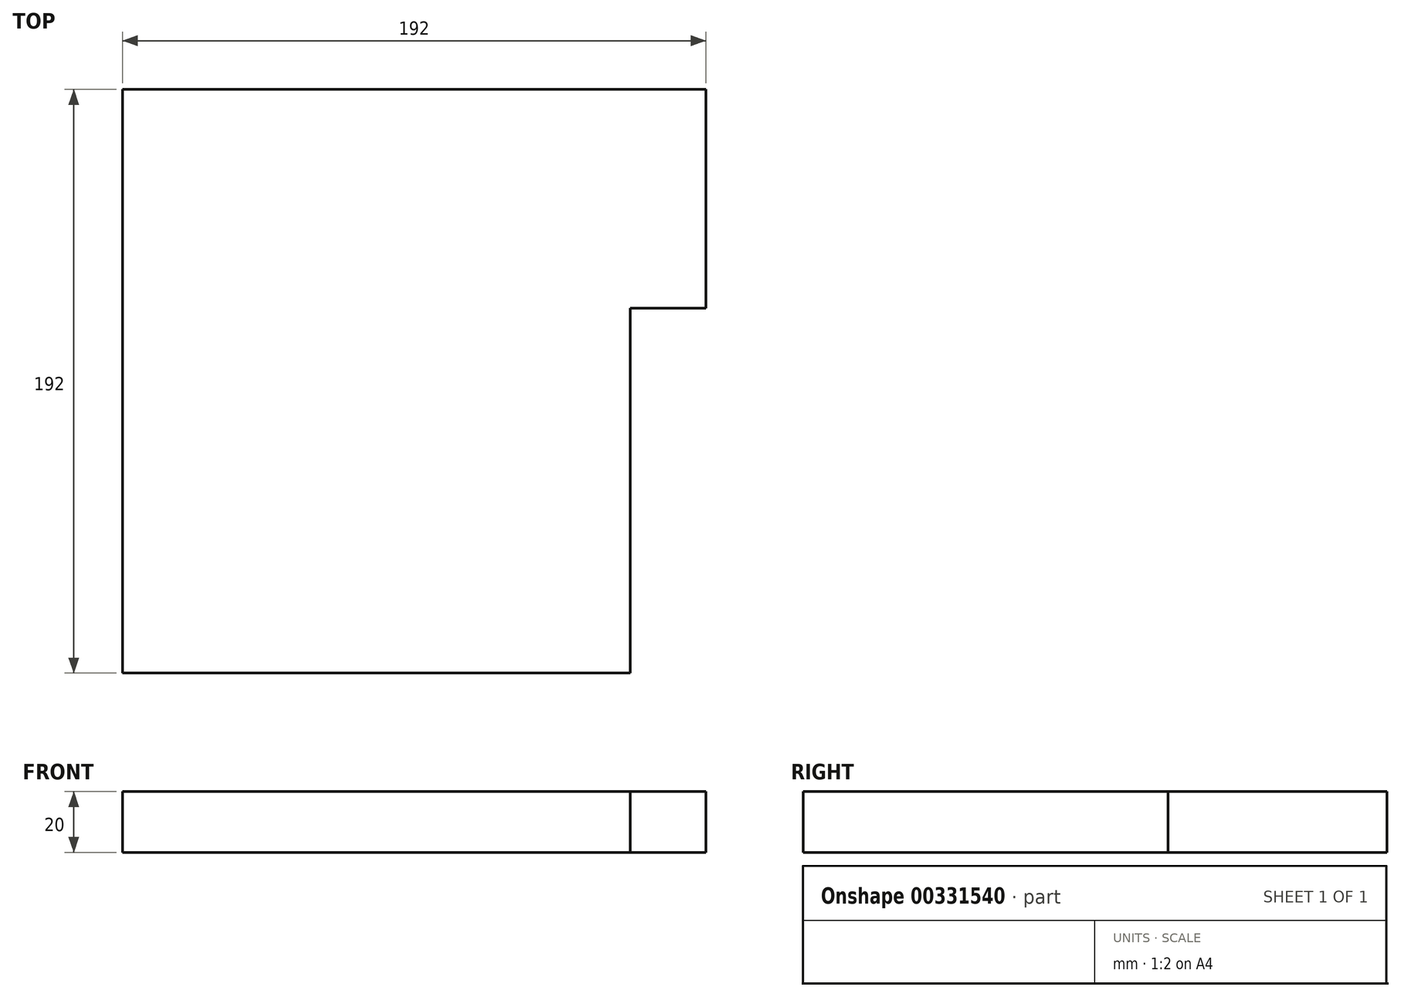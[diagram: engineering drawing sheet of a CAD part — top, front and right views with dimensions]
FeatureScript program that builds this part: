
annotation { "Feature Type Name" : "Feature", "Feature Type Description" : "" }
export const myFeature = defineFeature(function(context is Context, id is Id, definition is map)
    precondition{}
    {
        {
            var Q0;
            Q0=qCreatedBy(makeId("Top.planeOp"),FACE);
            var sketch = newSketch(context, id + "F0", { "sketchPlane" : qUnion([Q0])});
            skLineSegment(sketch, "E0", {"start": v(1313, 440) * mm, "end": v(1313, 406) * mm});
            skLineSegment(sketch, "E1", {"start": v(1313, -267) * mm, "end": v(1313, -301) * mm});
            skLineSegment(sketch, "E2", {"start": v(1313, -301) * mm, "end": v(647, -301) * mm});
            skLineSegment(sketch, "E3", {"start": v(1279, -267) * mm, "end": v(647, -267) * mm});
            skLineSegment(sketch, "E4", {"start": v(1279, 406) * mm, "end": v(688, 406) * mm});
            skLineSegment(sketch, "E5", {"start": v(688, 406) * mm, "end": v(688, -75) * mm});
            skLineSegment(sketch, "E6", {"start": v(688, -75) * mm, "end": v(413, -75) * mm});
            skLineSegment(sketch, "E7", {"start": v(647, -301) * mm, "end": v(647, -267) * mm});
            skLineSegment(sketch, "E8", {"start": v(536, -301) * mm, "end": v(536, -267) * mm});
            skLineSegment(sketch, "E9", {"start": v(536, -267) * mm, "end": v(328, -267) * mm});
            skLineSegment(sketch, "E10", {"start": v(328, -267) * mm, "end": v(328, -407) * mm});
            skLineSegment(sketch, "E11", {"start": v(328, -407) * mm, "end": v(-40, -407) * mm});
            skLineSegment(sketch, "E12", {"start": v(-40, -407) * mm, "end": v(-40, -188) * mm});
            skLineSegment(sketch, "E13", {"start": v(-40, -188) * mm, "end": v(-105, -188) * mm});
            skLineSegment(sketch, "E14", {"start": v(536, -301) * mm, "end": v(362, -301) * mm});
            skLineSegment(sketch, "E15", {"start": v(362, -301) * mm, "end": v(362, -440) * mm});
            skLineSegment(sketch, "E16", {"start": v(-60, -407) * mm, "end": v(-60, -215) * mm});
            skLineSegment(sketch, "E17", {"start": v(-60, -215) * mm, "end": v(-105, -215) * mm});
            skLineSegment(sketch, "E18", {"start": v(-105, -188) * mm, "end": v(-105, -215) * mm});
            skLineSegment(sketch, "E19", {"start": v(-60, -407) * mm, "end": v(-282, -407) * mm});
            skLineSegment(sketch, "E20", {"start": v(-282, -407) * mm, "end": v(-282, -287) * mm});
            skLineSegment(sketch, "E21", {"start": v(-282, -287) * mm, "end": v(-330, -287) * mm});
            skLineSegment(sketch, "E22", {"start": v(-330, -287) * mm, "end": v(-330, -407) * mm});
            skLineSegment(sketch, "E23", {"start": v(-330, -407) * mm, "end": v(-497, -407) * mm});
            skLineSegment(sketch, "E24", {"start": v(-197, -188) * mm, "end": v(-197, -215) * mm});
            skLineSegment(sketch, "E25", {"start": v(-197, -188) * mm, "end": v(-765, -188) * mm});
            skLineSegment(sketch, "E26", {"start": v(-197, -215) * mm, "end": v(-497, -215) * mm});
            skLineSegment(sketch, "E27", {"start": v(-497, -215) * mm, "end": v(-497, -231) * mm});
            skLineSegment(sketch, "E28", {"start": v(-497, -231) * mm, "end": v(-497, -293) * mm});
            skLineSegment(sketch, "E29", {"start": v(-497, -407) * mm, "end": v(-497, -349) * mm});
            skLineSegment(sketch, "E30", {"start": v(413, -75) * mm, "end": v(413, -54) * mm});
            skLineSegment(sketch, "E31", {"start": v(413, -54) * mm, "end": v(667, -54) * mm});
            skLineSegment(sketch, "E32", {"start": v(667, -54) * mm, "end": v(667, 406) * mm});
            skLineSegment(sketch, "E33", {"start": v(667, 406) * mm, "end": v(495, 406) * mm});
            skLineSegment(sketch, "E34", {"start": v(312, 406) * mm, "end": v(391, 406) * mm});
            skLineSegment(sketch, "E35", {"start": v(391, 406) * mm, "end": v(391, 440) * mm});
            skLineSegment(sketch, "E36", {"start": v(495, 406) * mm, "end": v(495, 440) * mm});
            skLineSegment(sketch, "E37", {"start": v(1313, 440) * mm, "end": v(495, 440) * mm});
            skLineSegment(sketch, "E38", {"start": v(312, -75) * mm, "end": v(60, -75) * mm});
            skLineSegment(sketch, "E39", {"start": v(-1279, 406) * mm, "end": v(-1279, 7) * mm});
            skLineSegment(sketch, "E40", {"start": v(-790, 406) * mm, "end": v(-790, 7) * mm});
            skLineSegment(sketch, "E41", {"start": v(-1279, 7) * mm, "end": v(-910, 7) * mm});
            skLineSegment(sketch, "E42", {"start": v(-790, 7) * mm, "end": v(-808, 7) * mm});
            skLineSegment(sketch, "E43", {"start": v(-765, -188) * mm, "end": v(-765, -208) * mm});
            skLineSegment(sketch, "E44", {"start": v(290, 141) * mm, "end": v(290, 406) * mm});
            skLineSegment(sketch, "E45", {"start": v(290, 141) * mm, "end": v(75, 141) * mm});
            skLineSegment(sketch, "E46", {"start": v(75, -46) * mm, "end": v(75, 141) * mm});
            skLineSegment(sketch, "E47", {"start": v(60, -75) * mm, "end": v(60, -46) * mm});
            skLineSegment(sketch, "E48", {"start": v(391, 406) * mm, "end": v(312, 406) * mm});
            skLineSegment(sketch, "E49", {"start": v(-139, 406) * mm, "end": v(-139, 440) * mm});
            skLineSegment(sketch, "E50", {"start": v(-318, 406) * mm, "end": v(-318, 440) * mm});
            skLineSegment(sketch, "E51", {"start": v(-515, 406) * mm, "end": v(-515, 440) * mm});
            skLineSegment(sketch, "E52", {"start": v(-694, 406) * mm, "end": v(-694, 440) * mm});
            skLineSegment(sketch, "E53", {"start": v(-770, 406) * mm, "end": v(-770, 9) * mm});
            skLineSegment(sketch, "E54", {"start": v(-694, 406) * mm, "end": v(-770, 406) * mm});
            skLineSegment(sketch, "E55", {"start": v(75, 406) * mm, "end": v(-139, 406) * mm});
            skLineSegment(sketch, "E56", {"start": v(-318, 406) * mm, "end": v(-515, 406) * mm});
            skLineSegment(sketch, "E57", {"start": v(-318, 440) * mm, "end": v(-515, 440) * mm});
            skLineSegment(sketch, "E58", {"start": v(-770, 9) * mm, "end": v(-754, 9) * mm});
            skLineSegment(sketch, "E59", {"start": v(-677, 9) * mm, "end": v(-659, 9) * mm});
            skLineSegment(sketch, "E60", {"start": v(-659, 9) * mm, "end": v(-659, -5) * mm});
            skLineSegment(sketch, "E61", {"start": v(-659, -5) * mm, "end": v(-659, -46) * mm});
            skLineSegment(sketch, "E62", {"start": v(-659, -46) * mm, "end": v(-60, -46) * mm});
            skLineSegment(sketch, "E63", {"start": v(-60, -75) * mm, "end": v(-60, -46) * mm});
            skLineSegment(sketch, "E64", {"start": v(60, -75) * mm, "end": v(128, -75) * mm});
            skLineSegment(sketch, "E65", {"start": v(60, -46) * mm, "end": v(75, -46) * mm});
            skLineSegment(sketch, "E66", {"start": v(96, -46) * mm, "end": v(290, -46) * mm});
            skLineSegment(sketch, "E67", {"start": v(-60, -75) * mm, "end": v(-677, -75) * mm});
            skLineSegment(sketch, "E68", {"start": v(-677, 9) * mm, "end": v(-677, -75) * mm});
            skLineSegment(sketch, "E69", {"start": v(-754, 9) * mm, "end": v(-754, -13) * mm});
            skLineSegment(sketch, "E70", {"start": v(-808, 7) * mm, "end": v(-808, -13) * mm});
            skLineSegment(sketch, "E71", {"start": v(-808, -13) * mm, "end": v(-754, -13) * mm});
            skLineSegment(sketch, "E72", {"start": v(-910, 7) * mm, "end": v(-910, -29) * mm});
            skLineSegment(sketch, "E73", {"start": v(-1279, -406) * mm, "end": v(-935, -406) * mm});
            skLineSegment(sketch, "E74", {"start": v(-1313, -440) * mm, "end": v(-935, -440) * mm});
            skLineSegment(sketch, "E75", {"start": v(-910, -29) * mm, "end": v(-935, -29) * mm});
            skLineSegment(sketch, "E76", {"start": v(-935, -13) * mm, "end": v(-1279, -13) * mm});
            skLineSegment(sketch, "E77", {"start": v(-910, -132) * mm, "end": v(-935, -132) * mm});
            skLineSegment(sketch, "E78", {"start": v(-910, -29) * mm, "end": v(-910, -13) * mm});
            skLineSegment(sketch, "E79", {"start": v(-935, -406) * mm, "end": v(-935, -132) * mm});
            skLineSegment(sketch, "E80", {"start": v(-935, -29) * mm, "end": v(-935, -13) * mm});
            skLineSegment(sketch, "E81", {"start": v(-877, -208) * mm, "end": v(-877, -188) * mm});
            skLineSegment(sketch, "E82", {"start": v(-910, -132) * mm, "end": v(-910, -188) * mm});
            skLineSegment(sketch, "E83", {"start": v(-877, -188) * mm, "end": v(-910, -188) * mm});
            skLineSegment(sketch, "E84", {"start": v(-877, -208) * mm, "end": v(-904, -208) * mm});
            skLineSegment(sketch, "E85", {"start": v(-904, -208) * mm, "end": v(-904, -406) * mm});
            skLineSegment(sketch, "E86", {"start": v(-904, -406) * mm, "end": v(-648, -406) * mm});
            skLineSegment(sketch, "E87", {"start": v(-765, -208) * mm, "end": v(-648, -208) * mm});
            skLineSegment(sketch, "E88", {"start": v(-648, -208) * mm, "end": v(-648, -273) * mm});
            skLineSegment(sketch, "E89", {"start": v(-648, -406) * mm, "end": v(-648, -343) * mm});
            skLineSegment(sketch, "E90", {"start": v(-935, -440) * mm, "end": v(362, -440) * mm});
            skLineSegment(sketch, "E91", {"start": v(151, 406) * mm, "end": v(151, 440) * mm});
            skLineSegment(sketch, "E92", {"start": v(224, 406) * mm, "end": v(224, 440) * mm});
            skLineSegment(sketch, "E93", {"start": v(290, 406) * mm, "end": v(224, 406) * mm});
            skLineSegment(sketch, "E94", {"start": v(151, 406) * mm, "end": v(96, 406) * mm});
            skLineSegment(sketch, "E95", {"start": v(391, 440) * mm, "end": v(224, 440) * mm});
            skLineSegment(sketch, "E96", {"start": v(151, 440) * mm, "end": v(-139, 440) * mm});
            skLineSegment(sketch, "E97", {"start": v(-907, 406) * mm, "end": v(-907, 440) * mm});
            skLineSegment(sketch, "E98", {"start": v(-1085, 406) * mm, "end": v(-1085, 440) * mm});
            skLineSegment(sketch, "E99", {"start": v(-790, 406) * mm, "end": v(-907, 406) * mm});
            skLineSegment(sketch, "E100", {"start": v(-1085, 406) * mm, "end": v(-1279, 406) * mm});
            skLineSegment(sketch, "E101", {"start": v(-694, 440) * mm, "end": v(-907, 440) * mm});
            skLineSegment(sketch, "E102", {"start": v(-1085, 440) * mm, "end": v(-1313, 440) * mm});
            skLineSegment(sketch, "E103", {"start": v(-1279, -118) * mm, "end": v(-1313, -118) * mm});
            skLineSegment(sketch, "E104", {"start": v(-1279, -297) * mm, "end": v(-1313, -297) * mm});
            skLineSegment(sketch, "E105", {"start": v(-1279, -13) * mm, "end": v(-1279, -118) * mm});
            skLineSegment(sketch, "E106", {"start": v(-1279, -297) * mm, "end": v(-1279, -406) * mm});
            skLineSegment(sketch, "E107", {"start": v(-1313, 440) * mm, "end": v(-1313, -118) * mm});
            skLineSegment(sketch, "E108", {"start": v(-1313, -297) * mm, "end": v(-1313, -440) * mm});
            skLineSegment(sketch, "E109", {"start": v(-648, -273) * mm, "end": v(-630, -273) * mm});
            skLineSegment(sketch, "E110", {"start": v(-648, -343) * mm, "end": v(-630, -343) * mm});
            skLineSegment(sketch, "E111", {"start": v(-515, -349) * mm, "end": v(-497, -349) * mm});
            skLineSegment(sketch, "E112", {"start": v(-515, -293) * mm, "end": v(-497, -293) * mm});
            skLineSegment(sketch, "E113", {"start": v(-515, -349) * mm, "end": v(-515, -406) * mm});
            skLineSegment(sketch, "E114", {"start": v(-630, -343) * mm, "end": v(-630, -406) * mm});
            skLineSegment(sketch, "E115", {"start": v(-630, -406) * mm, "end": v(-515, -406) * mm});
            skLineSegment(sketch, "E116", {"start": v(-630, -273) * mm, "end": v(-630, -206) * mm});
            skLineSegment(sketch, "E117", {"start": v(-630, -206) * mm, "end": v(-515, -206) * mm});
            skLineSegment(sketch, "E118", {"start": v(-515, -293) * mm, "end": v(-515, -206) * mm});
            skLineSegment(sketch, "E119", {"start": v(290, 43) * mm, "end": v(312, 43) * mm});
            skLineSegment(sketch, "E120", {"start": v(290, 124) * mm, "end": v(312, 124) * mm});
            skLineSegment(sketch, "E121", {"start": v(312, -75) * mm, "end": v(312, 43) * mm});
            skLineSegment(sketch, "E122", {"start": v(312, 124) * mm, "end": v(312, 406) * mm});
            skLineSegment(sketch, "E123", {"start": v(290, -46) * mm, "end": v(290, 43) * mm});
            skLineSegment(sketch, "E124", {"start": v(96, 222) * mm, "end": v(75, 222) * mm});
            skLineSegment(sketch, "E125", {"start": v(96, 222) * mm, "end": v(96, 406) * mm});
            skLineSegment(sketch, "E126", {"start": v(75, 222) * mm, "end": v(75, 406) * mm});
            skLineSegment(sketch, "E127", {"start": v(96, -46) * mm, "end": v(96, 124) * mm});
            skLineSegment(sketch, "E128", {"start": v(290, 124) * mm, "end": v(96, 124) * mm});
            skLineSegment(sketch, "E129", {"start": v(1279, -219) * mm, "end": v(1313, -219) * mm});
            skLineSegment(sketch, "E130", {"start": v(1279, -26) * mm, "end": v(1313, -26) * mm});
            skLineSegment(sketch, "E131", {"start": v(1279, 46) * mm, "end": v(1313, 46) * mm});
            skLineSegment(sketch, "E132", {"start": v(1279, 239) * mm, "end": v(1313, 239) * mm});
            skLineSegment(sketch, "E133", {"start": v(1313, 406) * mm, "end": v(1313, 239) * mm});
            skLineSegment(sketch, "E134", {"start": v(1279, 406) * mm, "end": v(1279, 239) * mm});
            skLineSegment(sketch, "E135", {"start": v(1313, 46) * mm, "end": v(1313, -26) * mm});
            skLineSegment(sketch, "E136", {"start": v(1313, -219) * mm, "end": v(1313, -267) * mm});
            skLineSegment(sketch, "E137", {"start": v(1279, 46) * mm, "end": v(1279, -26) * mm});
            skLineSegment(sketch, "E138", {"start": v(1279, -219) * mm, "end": v(1279, -267) * mm});
            skLineSegment(sketch, "E139", {"start": v(1313, -301) * mm, "end": v(1313, 440) * mm});
            skLineSegment(sketch, "E140", {"start": v(1313, -301) * mm, "end": v(362, -301) * mm});
            skLineSegment(sketch, "E141", {"start": v(362, -440) * mm, "end": v(-1313, -440) * mm});
            skLineSegment(sketch, "E142", {"start": v(-1313, 440) * mm, "end": v(-1313, -440) * mm});
            skLineSegment(sketch, "E143", {"start": v(-1313, 440) * mm, "end": v(1313, 440) * mm});
            skLineSegment(sketch, "E144", {"start": v(-321.5, -37.21) * mm, "end": v(-321.5, 162.79) * mm});
            skLineSegment(sketch, "E145", {"start": v(-321.5, -37.21) * mm, "end": v(-511.5, -37.21) * mm});
            skLineSegment(sketch, "E146", {"start": v(-321.5, 162.79) * mm, "end": v(-511.5, 162.79) * mm});
            skLineSegment(sketch, "E147", {"start": v(-511.5, -37.21) * mm, "end": v(-511.5, 162.79) * mm});
            skLineSegment(sketch, "E148", {"start": v(-321.5, -29.2) * mm, "end": v(-511.5, -29.2) * mm});
            skLineSegment(sketch, "E149", {"start": v(-499.08, -21.75) * mm, "end": v(-430.85, -21.75) * mm});
            skLineSegment(sketch, "E150", {"start": v(-430.85, -21.75) * mm, "end": v(-430.85, 2.94) * mm});
            skLineSegment(sketch, "E151", {"start": v(-430.85, 2.94) * mm, "end": v(-499.08, 2.94) * mm});
            skLineSegment(sketch, "E152", {"start": v(-499.08, 2.94) * mm, "end": v(-499.08, -21.75) * mm});
            skLineSegment(sketch, "E153", {"start": v(-333.92, -21.75) * mm, "end": v(-402.15, -21.75) * mm});
            skLineSegment(sketch, "E154", {"start": v(-402.15, -21.75) * mm, "end": v(-402.15, 2.94) * mm});
            skLineSegment(sketch, "E155", {"start": v(-402.15, 2.94) * mm, "end": v(-333.92, 2.94) * mm});
            skLineSegment(sketch, "E156", {"start": v(-333.92, 2.94) * mm, "end": v(-333.92, -21.75) * mm});
            skLineSegment(sketch, "E157", {"start": v(-321.5, 13.1) * mm, "end": v(-416.5, 13.1) * mm});
            skLineSegment(sketch, "E158", {"start": v(-511.5, 36.6) * mm, "end": v(-491.94, 63.04) * mm});
            skLineSegment(sketch, "E159", {"start": v(-491.94, 63.04) * mm, "end": v(-416.5, 13.1) * mm});
            skLineSegment(sketch, "E160", {"start": v(-416.5, 13.1) * mm, "end": v(-511.5, 36.6) * mm});
            skLineSegment(sketch, "E161", {"start": v(-321.5, 159.23) * mm, "end": v(-511.5, 159.23) * mm});
            skLineSegment(sketch, "E162", {"start": v(-552.43, 3.31) * mm, "end": v(-520.43, 3.31) * mm});
            skLineSegment(sketch, "E163", {"start": v(-552.43, 3.31) * mm, "end": v(-552.43, -36.7) * mm});
            skLineSegment(sketch, "E164", {"start": v(-520.43, 3.31) * mm, "end": v(-520.43, -36.7) * mm});
            skLineSegment(sketch, "E165", {"start": v(-552.43, -36.7) * mm, "end": v(-520.43, -36.7) * mm});
            skLineSegment(sketch, "E166", {"start": v(-552.43, -6.69) * mm, "end": v(-520.43, -6.69) * mm});
            skLineSegment(sketch, "E167", {"start": v(-552.43, -3.69) * mm, "end": v(-520.43, -3.69) * mm});
            skLineSegment(sketch, "E168", {"start": v(-552.43, -0.69) * mm, "end": v(-520.43, -0.69) * mm});
            skLineSegment(sketch, "E169", {"start": v(-552.43, 2.31) * mm, "end": v(-520.43, 2.31) * mm});
            skLineSegment(sketch, "E170", {"start": v(-280.57, 3.31) * mm, "end": v(-312.57, 3.31) * mm});
            skLineSegment(sketch, "E171", {"start": v(-280.57, 3.31) * mm, "end": v(-280.57, -36.7) * mm});
            skLineSegment(sketch, "E172", {"start": v(-312.57, 3.31) * mm, "end": v(-312.57, -36.7) * mm});
            skLineSegment(sketch, "E173", {"start": v(-280.57, -36.7) * mm, "end": v(-312.57, -36.7) * mm});
            skLineSegment(sketch, "E174", {"start": v(-280.57, -6.69) * mm, "end": v(-312.57, -6.69) * mm});
            skLineSegment(sketch, "E175", {"start": v(-280.57, -3.69) * mm, "end": v(-312.57, -3.69) * mm});
            skLineSegment(sketch, "E176", {"start": v(-280.57, -0.69) * mm, "end": v(-312.57, -0.69) * mm});
            skLineSegment(sketch, "E177", {"start": v(-280.57, 2.31) * mm, "end": v(-312.57, 2.31) * mm});
            skLineSegment(sketch, "E178", {"start": v(-765, 395.6) * mm, "end": v(-765, 20.6) * mm});
            skLineSegment(sketch, "E179", {"start": v(-765, 395.6) * mm, "end": v(-705, 395.6) * mm});
            skLineSegment(sketch, "E180", {"start": v(-705, 395.6) * mm, "end": v(-705, 20.6) * mm});
            skLineSegment(sketch, "E181", {"start": v(-765, 20.6) * mm, "end": v(-705, 20.6) * mm});
            skLineSegment(sketch, "E182", {"start": v(-705, 395.6) * mm, "end": v(-700, 395.6) * mm});
            skLineSegment(sketch, "E183", {"start": v(-700, 395.6) * mm, "end": v(-700, 20.6) * mm});
            skLineSegment(sketch, "E184", {"start": v(-705, 20.6) * mm, "end": v(-700, 20.6) * mm});
            skLineSegment(sketch, "E185", {"start": v(-705, 114.35) * mm, "end": v(-700, 114.35) * mm});
            skLineSegment(sketch, "E186", {"start": v(-705, 301.85) * mm, "end": v(-700, 301.85) * mm});
            skLineSegment(sketch, "E187", {"start": v(-705, 208.1) * mm, "end": v(-700, 208.1) * mm});
            skLineSegment(sketch, "E188", {"start": v(-705, 348.73) * mm, "end": v(-700, 348.73) * mm});
            skLineSegment(sketch, "E189", {"start": v(-705, 67.47) * mm, "end": v(-700, 67.47) * mm});
            skSolve(sketch);
        }
        {
            var Q0;
            Q0=makeQuery(id+"F0.imprint","IMPRINT",FACE,{"disambiguationData":[TD([[makeQuery(id+"F0.imprint","IMPRINT",EDGE,{"derivedFrom":sQuery(id+"F0.wireOp",EDGE,"E3")}),-1.0]])]});
            var sketch = newSketch(context, id + "F1", { "sketchPlane" : qUnion([Q0])});
            skLineSegment(sketch, "E190.0", {"start": v(-497, -231) * mm, "end": v(-497, -293) * mm});
            skLineSegment(sketch, "E191.0", {"start": v(-330, -215) * mm, "end": v(-497, -215) * mm});
            skLineSegment(sketch, "E192.0", {"start": v(-330, -287) * mm, "end": v(-330, -407) * mm});
            skLineSegment(sketch, "E193.0", {"start": v(-330, -407) * mm, "end": v(-497, -407) * mm});
            skLineSegment(sketch, "E194", {"start": v(-330, -287) * mm, "end": v(-330, -215) * mm});
            skLineSegment(sketch, "E195", {"start": v(-497, -215) * mm, "end": v(-497, -231) * mm});
            skLineSegment(sketch, "E196", {"start": v(-497, -293) * mm, "end": v(-497, -407) * mm});
            skPoint(sketch, "E197.orphan", {"position": v(-197, -215) * mm});
            skSolve(sketch);
        }
        {
            var Q0;
            Q0=qSketchRegion(id+"F1",true);
            extrude(context, id + "F2", {"entities" : qUnion([Q0]), "depth" : 20 * mm});
        }
        {
            var Q0;
            Q0=makeQuery(id+"F0.imprint","IMPRINT",FACE,{"disambiguationData":[TD([[makeQuery(id+"F0.imprint","IMPRINT",EDGE,{"derivedFrom":sQuery(id+"F0.wireOp",EDGE,"E3")}),-1.0]])]});
            var sketch = newSketch(context, id + "F3", { "sketchPlane" : qUnion([Q0])});
            skLineSegment(sketch, "E198.0", {"start": v(-522, -190) * mm, "end": v(-522, -432) * mm});
            skLineSegment(sketch, "E198.1", {"start": v(-305, -190) * mm, "end": v(-522, -190) * mm});
            skLineSegment(sketch, "E198.2", {"start": v(-305, -432) * mm, "end": v(-305, -190) * mm});
            skLineSegment(sketch, "E198.3", {"start": v(-522, -432) * mm, "end": v(-305, -432) * mm});
            skLineSegment(sketch, "E199.0.0", {"start": v(-497, -215) * mm, "end": v(-497, -407) * mm});
            skLineSegment(sketch, "E199.0.1", {"start": v(-497, -407) * mm, "end": v(-330, -407) * mm});
            skLineSegment(sketch, "E199.0.2", {"start": v(-330, -407) * mm, "end": v(-330, -215) * mm});
            skLineSegment(sketch, "E199.0.3", {"start": v(-330, -215) * mm, "end": v(-497, -215) * mm});
            skSolve(sketch);
        }
        {
            var Q0;
            Q0=qSketchRegion(id+"F3",true);
            extrude(context, id + "F4", {"entities" : qUnion([Q0]), "operationType" : NewBodyOperationType.ADD, "depth" : (220 + 20) * mm});
        }
        {
            var Q0;
            Q0=makeQuery(id+"F2.opExtrude","CAP_FACE",FACE,{"disambiguationData":[OSD([sQuery(id+"F1.wireOp",EDGE,"E190.0"),sQuery(id+"F1.wireOp",EDGE,"E191.0"),sQuery(id+"F1.wireOp",EDGE,"E192.0"),sQuery(id+"F1.wireOp",EDGE,"E193.0"),sQuery(id+"F1.wireOp",EDGE,"E194"),sQuery(id+"F1.wireOp",EDGE,"E195"),sQuery(id+"F1.wireOp",EDGE,"E196")])],"isStart":false});
            var sketch = newSketch(context, id + "F5", { "sketchPlane" : qUnion([Q0])});
            skLineSegment(sketch, "E200.0", {"start": v(-282, -287) * mm, "end": v(-330, -287) * mm});
            skLineSegment(sketch, "E201.0", {"start": v(-282, -215) * mm, "end": v(-330, -215) * mm});
            skLineSegment(sketch, "E202", {"start": v(-330, -287) * mm, "end": v(-330, -215) * mm});
            skLineSegment(sketch, "E203", {"start": v(-282, -287) * mm, "end": v(-282, -215) * mm});
            skPoint(sketch, "E204.orphan", {"position": v(-197, -215) * mm});
            skPoint(sketch, "E205.orphan", {"position": v(-497, -215) * mm});
            skSolve(sketch);
        }
        {
            var Q0;
            Q0=qSketchRegion(id+"F5",true);
            extrude(context, id + "F6", {"entities" : qUnion([Q0]), "operationType" : NewBodyOperationType.REMOVE, "depth" : 250 * mm});
        }
        {
            var Q0;
            Q0=makeQuery(id+"F4.opExtrude","SWEPT_FACE",FACE,{"disambiguationData":[OSD([sQuery(id+"F3.wireOp",EDGE,"E199.0.0")])]});
            var sketch = newSketch(context, id + "F7", { "sketchPlane" : qUnion([Q0])});
            skLineSegment(sketch, "E206.0", {"start": v(-407, 0) * mm, "end": v(-349, 0) * mm});
            skLineSegment(sketch, "E207", {"start": v(-270, 220) * mm, "end": v(-349, 220) * mm});
            skLineSegment(sketch, "E208", {"start": v(-349, 220) * mm, "end": v(-349, 135) * mm});
            skLineSegment(sketch, "E209", {"start": v(-349, 135) * mm, "end": v(-270, 135) * mm});
            skLineSegment(sketch, "E210", {"start": v(-270, 135) * mm, "end": v(-270, 220) * mm});
            skSolve(sketch);
        }
        {
            var Q0;
            Q0=qSketchRegion(id+"F7",true);
            extrude(context, id + "F8", {"entities" : qUnion([Q0]), "operationType" : NewBodyOperationType.REMOVE, "oppositeDirection" : true, "depth" : 25 * mm});
        }
        {
            var Q0;
            Q0=makeQuery(id+"F4.opExtrude","SWEPT_FACE",FACE,{"disambiguationData":[OSD([sQuery(id+"F3.wireOp",EDGE,"E199.0.0")])]});
            var sketch = newSketch(context, id + "F9", { "sketchPlane" : qUnion([Q0])});
            skLineSegment(sketch, "E211", {"start": v(-270, 220) * mm, "end": v(-290, 220) * mm});
            skLineSegment(sketch, "E212.0", {"start": v(-270, 135) * mm, "end": v(-270, 220) * mm});
            skLineSegment(sketch, "E213.0", {"start": v(-349, 135) * mm, "end": v(-270, 135) * mm});
            skLineSegment(sketch, "E214", {"start": v(-290, 220) * mm, "end": v(-290, 155) * mm});
            skLineSegment(sketch, "E215", {"start": v(-349, 135) * mm, "end": v(-349, 155) * mm});
            skLineSegment(sketch, "E216", {"start": v(-349, 155) * mm, "end": v(-290, 155) * mm});
            skSolve(sketch);
        }
        {
            var Q0;
            Q0=qSketchRegion(id+"F9",true);
            var Q1;
            Q1=makeQuery(id+"F4.opExtrude","SWEPT_FACE",FACE,{"disambiguationData":[OSD([sQuery(id+"F3.wireOp",EDGE,"E198.0")])]});
            extrude(context, id + "F10", {"entities" : qUnion([Q0]), "operationType" : NewBodyOperationType.ADD, "endBound" : BoundingType.UP_TO_SURFACE, "oppositeDirection" : true, "endBoundEntityFace" : qUnion([Q1]), "depth" : 25 * mm});
        }
        {
            var Q0;
            Q0=makeQuery(id+"F4.opExtrude","CAP_FACE",FACE,{"disambiguationData":[OSD([sQuery(id+"F3.wireOp",EDGE,"E198.0"),sQuery(id+"F3.wireOp",EDGE,"E198.1"),sQuery(id+"F3.wireOp",EDGE,"E198.2"),sQuery(id+"F3.wireOp",EDGE,"E198.3"),sQuery(id+"F3.wireOp",EDGE,"E199.0.0"),sQuery(id+"F3.wireOp",EDGE,"E199.0.1"),sQuery(id+"F3.wireOp",EDGE,"E199.0.2"),sQuery(id+"F3.wireOp",EDGE,"E199.0.3")])],"isStart":false});
            var sketch = newSketch(context, id + "F11", { "sketchPlane" : qUnion([Q0])});
            skLineSegment(sketch, "E217.0.0", {"start": v(-497, -215) * mm, "end": v(-305, -215) * mm});
            skLineSegment(sketch, "E217.0.1", {"start": v(-305, -215) * mm, "end": v(-305, -190) * mm});
            skLineSegment(sketch, "E217.0.2", {"start": v(-305, -190) * mm, "end": v(-522, -190) * mm});
            skLineSegment(sketch, "E217.0.3", {"start": v(-522, -190) * mm, "end": v(-522, -432) * mm});
            skLineSegment(sketch, "E217.0.4", {"start": v(-522, -432) * mm, "end": v(-305, -432) * mm});
            skLineSegment(sketch, "E217.0.5", {"start": v(-305, -432) * mm, "end": v(-305, -287) * mm});
            skLineSegment(sketch, "E217.0.6", {"start": v(-305, -287) * mm, "end": v(-330, -287) * mm});
            skLineSegment(sketch, "E217.0.7", {"start": v(-330, -287) * mm, "end": v(-330, -407) * mm});
            skLineSegment(sketch, "E217.0.8", {"start": v(-330, -407) * mm, "end": v(-497, -407) * mm});
            skLineSegment(sketch, "E217.0.9", {"start": v(-497, -407) * mm, "end": v(-497, -215) * mm});
            skSolve(sketch);
        }
        {
            var Q0;
            Q0 = qSketchRegion(id + "F11", true);
            extrude(context, id + "F12", {"entities" : qUnion([Q0]), "operationType" : NewBodyOperationType.REMOVE, "endBound" : BoundingType.THROUGH_ALL, "oppositeDirection" : true, "depth" : 25 * mm});
        }
    });
